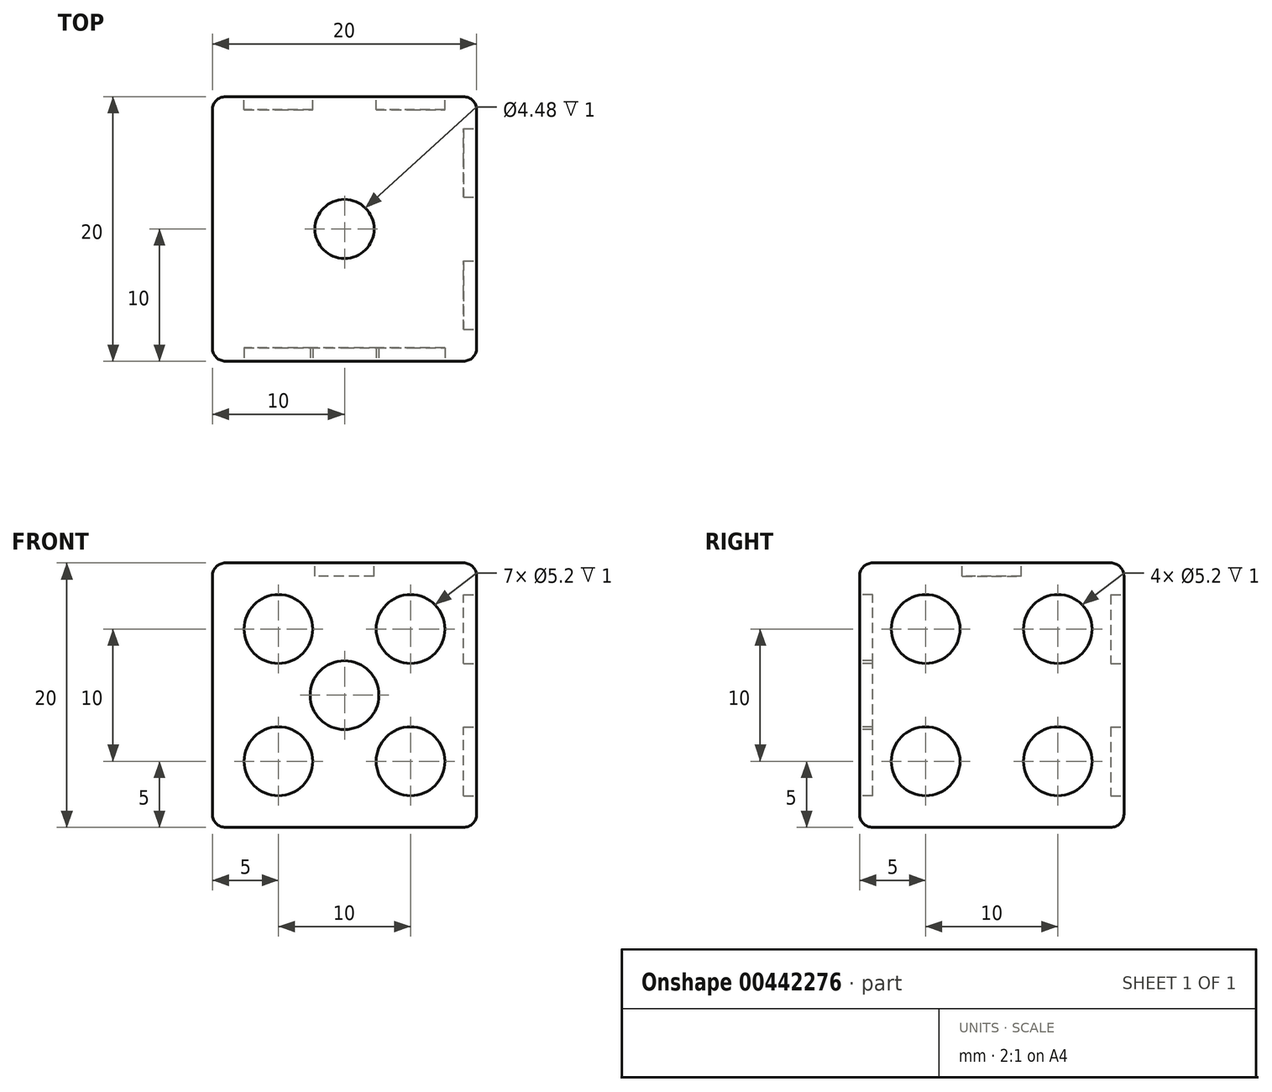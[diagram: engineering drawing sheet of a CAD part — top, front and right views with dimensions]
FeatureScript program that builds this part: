
annotation { "Feature Type Name" : "Feature", "Feature Type Description" : "" }
export const myFeature = defineFeature(function(context is Context, id is Id, definition is map)
    precondition{}
    {
        {
            var Q0;
            Q0=qCreatedBy(makeId("Front.planeOp"),FACE);
            var sketch = newSketch(context, id + "F0", { "sketchPlane" : qUnion([Q0])});
            skLineSegment(sketch, "E0.bottom", {"start": v(0, 0) * mm, "end": v(20, 0) * mm});
            skLineSegment(sketch, "E0.top", {"start": v(0, 20) * mm, "end": v(20, 20) * mm});
            skLineSegment(sketch, "E0.left", {"start": v(0, 0) * mm, "end": v(0, 20) * mm});
            skLineSegment(sketch, "E0.right", {"start": v(20, 0) * mm, "end": v(20, 20) * mm});
            skSolve(sketch);
        }
        {
            var Q0;
            Q0 = qSketchRegion(id + "F0", true);
            extrude(context, id + "F1", {"entities" : qUnion([Q0]), "depth" : 20 * mm});
        }
        {
            var Q0;
            Q0=makeQuery(id+"F1.opExtrude","CAP_FACE",FACE,{"disambiguationData":[OSD([sQuery(id+"F0.wireOp",EDGE,"E0.bottom"),sQuery(id+"F0.wireOp",EDGE,"E0.top"),sQuery(id+"F0.wireOp",EDGE,"E0.left"),sQuery(id+"F0.wireOp",EDGE,"E0.right")])],"isStart":false});
            var sketch = newSketch(context, id + "F2", { "sketchPlane" : qUnion([Q0])});
            skLineSegment(sketch, "E1", {"start": v(0, 20) * mm, "end": v(20, 0) * mm, "construction": true});
            skLineSegment(sketch, "E2", {"start": v(20, 0) * mm, "end": v(20, 20) * mm, "construction": true});
            skLineSegment(sketch, "E3", {"start": v(20, 20) * mm, "end": v(0, 0) * mm, "construction": true});
            skCircle(sketch, "E4", {"center": v(10, 10) * mm, "radius": 2.6 * mm});
            skCircle(sketch, "E5", {"center": v(5, 15) * mm, "radius": 2.6 * mm});
            skCircle(sketch, "E6.MirrorC", {"center": v(15, 5) * mm, "radius": 2.6 * mm});
            skLineSegment(sketch, "E7", {"start": v(10, 10) * mm, "end": v(10, 0) * mm, "construction": true});
            skCircle(sketch, "E8.MirrorC", {"center": v(15, 15) * mm, "radius": 2.6 * mm});
            skCircle(sketch, "E9.MirrorC", {"center": v(5, 5) * mm, "radius": 2.6 * mm});
            skSolve(sketch);
        }
        {
            var Q0;
            Q0 = qSketchRegion(id + "F2", true);
            extrude(context, id + "F3", {"entities" : qUnion([Q0]), "operationType" : NewBodyOperationType.REMOVE, "oppositeDirection" : true, "depth" : 1 * mm});
        }
        {
            var Q0;
            Q0=makeQuery(id+"F1.opExtrude","CAP_FACE",FACE,{"disambiguationData":[OSD([sQuery(id+"F0.wireOp",EDGE,"E0.bottom"),sQuery(id+"F0.wireOp",EDGE,"E0.top"),sQuery(id+"F0.wireOp",EDGE,"E0.left"),sQuery(id+"F0.wireOp",EDGE,"E0.right")])],"isStart":true});
            var sketch = newSketch(context, id + "F4", { "sketchPlane" : qUnion([Q0])});
            skLineSegment(sketch, "E10", {"start": v(0, 0) * mm, "end": v(-20, 20) * mm, "construction": true});
            skCircle(sketch, "E11", {"center": v(-5, 15) * mm, "radius": 2.6 * mm});
            skCircle(sketch, "E12.MirrorC", {"center": v(-15, 5) * mm, "radius": 2.6 * mm});
            skSolve(sketch);
        }
        {
            var Q0;
            Q0 = qSketchRegion(id + "F4", true);
            extrude(context, id + "F5", {"entities" : qUnion([Q0]), "operationType" : NewBodyOperationType.REMOVE, "oppositeDirection" : true, "depth" : 1 * mm});
        }
        {
            var Q0;
            Q0=makeQuery(id+"F1.opExtrude","SWEPT_FACE",FACE,{"disambiguationData":[OSD([sQuery(id+"F0.wireOp",EDGE,"E0.top")])]});
            var sketch = newSketch(context, id + "F6", { "sketchPlane" : qUnion([Q0])});
            skCircle(sketch, "E13", {"center": v(10, -10) * mm, "radius": 2.24 * mm});
            skPoint(sketch, "E13.centerSnap0", {"position": v(0, -10) * mm});
            skPoint(sketch, "E13.centerSnap1", {"position": v(10, -20) * mm});
            skSolve(sketch);
        }
        {
            var Q0;
            Q0 = qSketchRegion(id + "F6", true);
            extrude(context, id + "F7", {"entities" : qUnion([Q0]), "operationType" : NewBodyOperationType.REMOVE, "oppositeDirection" : true, "depth" : 1 * mm});
        }
        {
            var Q0;
            Q0=makeQuery(id+"F1.opExtrude","SWEPT_FACE",FACE,{"disambiguationData":[OSD([sQuery(id+"F0.wireOp",EDGE,"E0.right")])]});
            var sketch = newSketch(context, id + "F8", { "sketchPlane" : qUnion([Q0])});
            skLineSegment(sketch, "E14", {"start": v(-20, 10) * mm, "end": v(0, 10) * mm, "construction": true});
            skLineSegment(sketch, "E15", {"start": v(-10, 0) * mm, "end": v(-10, 23.1) * mm, "construction": true});
            skCircle(sketch, "E16", {"center": v(-15, 5) * mm, "radius": 2.6 * mm});
            skCircle(sketch, "E17.MirrorC", {"center": v(-15, 15) * mm, "radius": 2.6 * mm});
            skCircle(sketch, "E18.MirrorC", {"center": v(-5, 15) * mm, "radius": 2.6 * mm});
            skCircle(sketch, "E19.MirrorC", {"center": v(-5, 5) * mm, "radius": 2.6 * mm});
            skSolve(sketch);
        }
        {
            var Q0;
            Q0 = qSketchRegion(id + "F8", true);
            extrude(context, id + "F9", {"entities" : qUnion([Q0]), "operationType" : NewBodyOperationType.REMOVE, "oppositeDirection" : true, "depth" : 1 * mm});
        }
        {
            var Q0;
            Q0=makeQuery(id+"F1.opExtrude","CAP_EDGE",EDGE,{"disambiguationData":[OSD([sQuery(id+"F0.wireOp",EDGE,"E0.right")])],"isStart":true});
            var Q1;
            Q1=makeQuery(id+"F1.opExtrude","SWEPT_EDGE",EDGE,{"disambiguationData":[OSD([sQuery(id+"F0.wireOp",EDGE,"E0.top"),sQuery(id+"F0.wireOp",EDGE,"E0.right")])]});
            var Q2;
            Q2=makeQuery(id+"F1.opExtrude","CAP_EDGE",EDGE,{"disambiguationData":[OSD([sQuery(id+"F0.wireOp",EDGE,"E0.top")])],"isStart":true});
            var Q3;
            Q3=makeQuery(id+"F1.opExtrude","CAP_EDGE",EDGE,{"disambiguationData":[OSD([sQuery(id+"F0.wireOp",EDGE,"E0.left")])],"isStart":true});
            var Q4;
            Q4=makeQuery(id+"F1.opExtrude","SWEPT_EDGE",EDGE,{"disambiguationData":[OSD([sQuery(id+"F0.wireOp",EDGE,"E0.top"),sQuery(id+"F0.wireOp",EDGE,"E0.left")])]});
            var Q5;
            Q5=makeQuery(id+"F1.opExtrude","SWEPT_EDGE",EDGE,{"disambiguationData":[OSD([sQuery(id+"F0.wireOp",EDGE,"E0.bottom"),sQuery(id+"F0.wireOp",EDGE,"E0.right")])]});
            var Q6;
            Q6=makeQuery(id+"F1.opExtrude","CAP_EDGE",EDGE,{"disambiguationData":[OSD([sQuery(id+"F0.wireOp",EDGE,"E0.bottom")])],"isStart":true});
            var Q7;
            Q7=makeQuery(id+"F1.opExtrude","SWEPT_EDGE",EDGE,{"disambiguationData":[OSD([sQuery(id+"F0.wireOp",EDGE,"E0.bottom"),sQuery(id+"F0.wireOp",EDGE,"E0.left")])]});
            var Q8;
            Q8=makeQuery(id+"F1.opExtrude","CAP_EDGE",EDGE,{"disambiguationData":[OSD([sQuery(id+"F0.wireOp",EDGE,"E0.left")])],"isStart":false});
            var Q9;
            Q9=makeQuery(id+"F1.opExtrude","CAP_EDGE",EDGE,{"disambiguationData":[OSD([sQuery(id+"F0.wireOp",EDGE,"E0.bottom")])],"isStart":false});
            var Q10;
            Q10=makeQuery(id+"F1.opExtrude","CAP_EDGE",EDGE,{"disambiguationData":[OSD([sQuery(id+"F0.wireOp",EDGE,"E0.right")])],"isStart":false});
            var Q11;
            Q11=makeQuery(id+"F1.opExtrude","CAP_EDGE",EDGE,{"disambiguationData":[OSD([sQuery(id+"F0.wireOp",EDGE,"E0.top")])],"isStart":false});
            fillet(context, id + "F10", {"entities" : qUnion([Q0, Q1, Q2, Q3, Q4, Q5, Q6, Q7, Q8, Q9, Q10, Q11]), "radius" : 1 * mm, "tangentPropagation" : true, "allowEdgeOverflow" : false});
        }
    });
